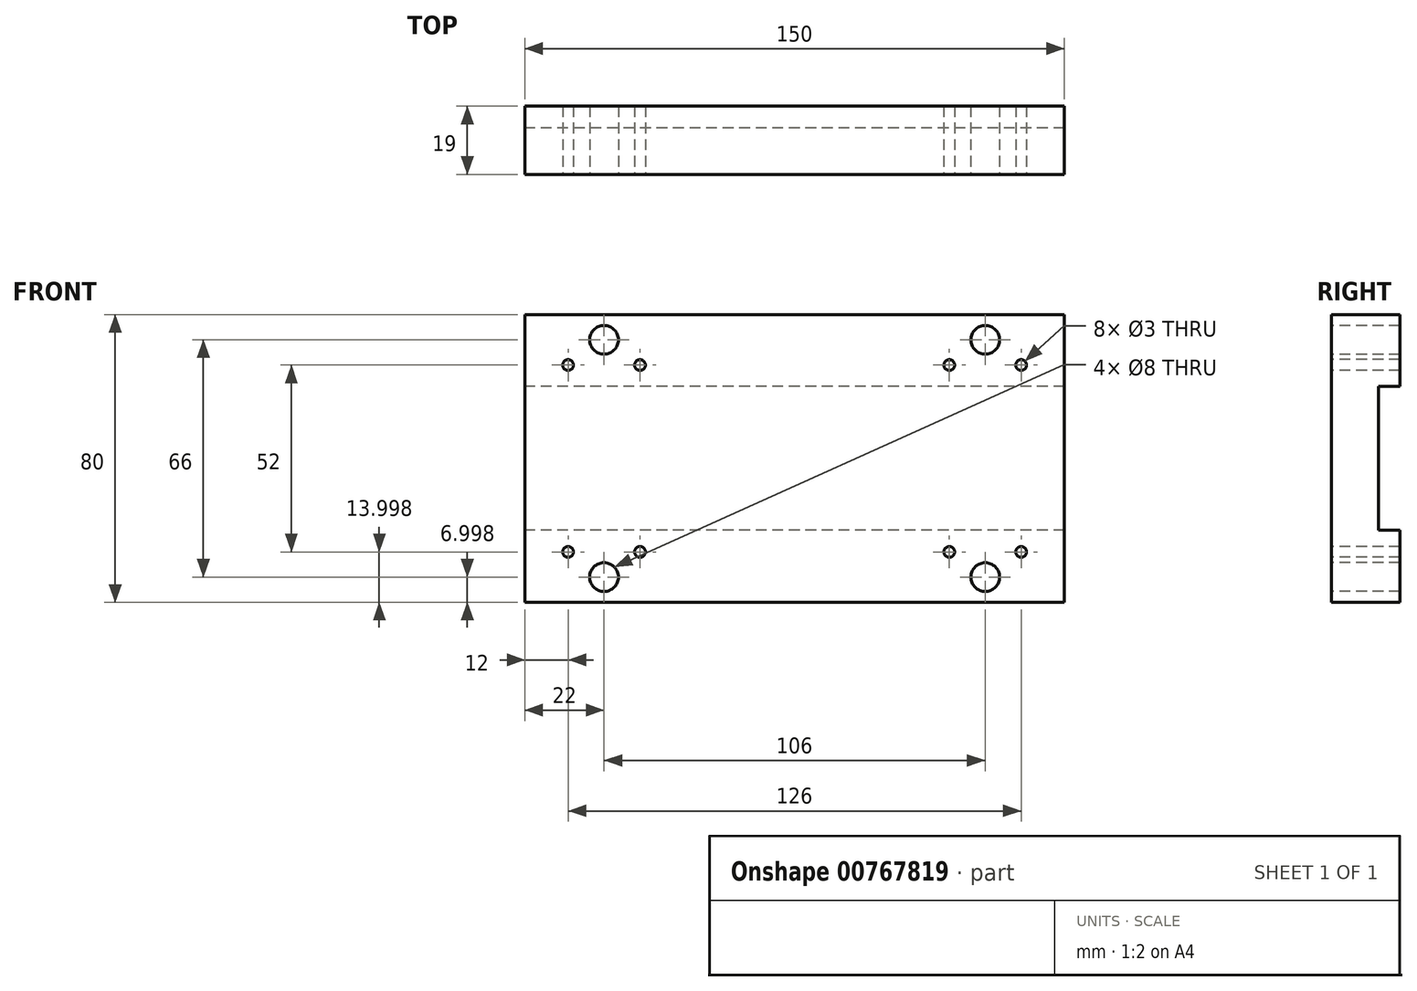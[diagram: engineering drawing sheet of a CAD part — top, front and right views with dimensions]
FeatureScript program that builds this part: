
annotation { "Feature Type Name" : "Feature", "Feature Type Description" : "" }
export const myFeature = defineFeature(function(context is Context, id is Id, definition is map)
    precondition{}
    {
        {
            var Q0;
            Q0=qCreatedBy(makeId("Right.planeOp"),FACE);
            var sketch = newSketch(context, id + "F0", { "sketchPlane" : qUnion([Q0])});
            skLineSegment(sketch, "E0.bottom", {"start": v(0, 43.24) * mm, "end": v(-19, 43.24) * mm});
            skLineSegment(sketch, "E0.top", {"start": v(0, -36.76) * mm, "end": v(-19, -36.76) * mm});
            skLineSegment(sketch, "E0.left", {"start": v(0, 43.24) * mm, "end": v(0, 23.24) * mm});
            skLineSegment(sketch, "E0.right", {"start": v(-19, 43.24) * mm, "end": v(-19, -36.76) * mm});
            skLineSegment(sketch, "E1.bottom", {"start": v(0, 23.24) * mm, "end": v(-6, 23.24) * mm});
            skLineSegment(sketch, "E1.top", {"start": v(0, -16.76) * mm, "end": v(-6, -16.76) * mm});
            skLineSegment(sketch, "E1.right", {"start": v(-6, 23.24) * mm, "end": v(-6, -16.76) * mm});
            skLineSegment(sketch, "E2.trimOffspring", {"start": v(0, -16.76) * mm, "end": v(0, -36.76) * mm});
            skSolve(sketch);
        }
        {
            var Q0;
            Q0=makeQuery(id+"F0.imprint","IMPRINT",FACE,{"disambiguationData":[TD([[makeQuery(id+"F0.imprint","IMPRINT",EDGE,{"derivedFrom":sQuery(id+"F0.wireOp",EDGE,"E0.bottom")}),1.0]])]});
            extrude(context, id + "F1", {"entities" : qUnion([Q0]), "depth" : 150 * mm, "offsetDistance" : 25 * mm});
        }
        {
            var Q0;
            Q0=makeQuery(id+"F1.opExtrude","SWEPT_FACE",FACE,{"disambiguationData":[OSD([sQuery(id+"F0.wireOp",EDGE,"E0.right")])]});
            var sketch = newSketch(context, id + "F2", { "sketchPlane" : qUnion([Q0])});
            skLineSegment(sketch, "E3", {"start": v(0, 29.24) * mm, "end": v(150, 29.24) * mm, "construction": true});
            skLineSegment(sketch, "E4", {"start": v(12, 43.24) * mm, "end": v(12, -36.76) * mm, "construction": true});
            skLineSegment(sketch, "E5", {"start": v(0, -22.76) * mm, "end": v(150, -22.76) * mm, "construction": true});
            skLineSegment(sketch, "E6", {"start": v(138, 43.24) * mm, "end": v(138, -36.76) * mm, "construction": true});
            skPoint(sketch, "E7", {"position": v(12, 29.24) * mm});
            skPoint(sketch, "E8", {"position": v(138, 29.24) * mm});
            skPoint(sketch, "E9", {"position": v(138, -22.76) * mm});
            skPoint(sketch, "E10", {"position": v(12, -22.76) * mm});
            skLineSegment(sketch, "E11", {"start": v(118, 43.24) * mm, "end": v(118, -36.76) * mm, "construction": true});
            skLineSegment(sketch, "E12", {"start": v(32, 43.24) * mm, "end": v(32, -36.76) * mm, "construction": true});
            skPoint(sketch, "E13", {"position": v(118, 29.24) * mm});
            skPoint(sketch, "E14", {"position": v(32, 29.24) * mm});
            skPoint(sketch, "E15", {"position": v(32, -22.76) * mm});
            skPoint(sketch, "E16", {"position": v(118, -22.76) * mm});
            skLineSegment(sketch, "E17", {"start": v(138, 43.24) * mm, "end": v(118, 29.24) * mm});
            skLineSegment(sketch, "E18", {"start": v(32, 29.24) * mm, "end": v(12, 43.24) * mm});
            skLineSegment(sketch, "E19", {"start": v(32, -22.76) * mm, "end": v(12, -36.76) * mm});
            skLineSegment(sketch, "E20", {"start": v(118, -22.76) * mm, "end": v(138, -36.76) * mm});
            skPoint(sketch, "E21", {"position": v(128, 36.24) * mm});
            skPoint(sketch, "E22", {"position": v(22, 36.24) * mm});
            skPoint(sketch, "E23", {"position": v(22, -29.76) * mm});
            skPoint(sketch, "E24", {"position": v(128, -29.76) * mm});
            skSolve(sketch);
        }
        {
            var Q0;
            Q0=sQuery(id+"F2.wireOp",VERTEX,"E7");
            var Q1;
            Q1=sQuery(id+"F2.wireOp",VERTEX,"E8");
            var Q2;
            Q2=sQuery(id+"F2.wireOp",VERTEX,"E10");
            var Q3;
            Q3=sQuery(id+"F2.wireOp",VERTEX,"E9");
            var Q4;
            Q4=sQuery(id+"F2.wireOp",VERTEX,"E13");
            var Q5;
            Q5=sQuery(id+"F2.wireOp",VERTEX,"E16");
            var Q6;
            Q6=sQuery(id+"F2.wireOp",VERTEX,"E14");
            var Q7;
            Q7=sQuery(id+"F2.wireOp",VERTEX,"E15");
            var Q8;
            Q8=makeQuery(id+"F1.opExtrude","SWEPT_BODY",BODY,{"disambiguationData":[OSD([sQuery(id+"F0.wireOp",EDGE,"E0.bottom"),sQuery(id+"F0.wireOp",EDGE,"E0.top"),sQuery(id+"F0.wireOp",EDGE,"E0.left"),sQuery(id+"F0.wireOp",EDGE,"E0.right"),sQuery(id+"F0.wireOp",EDGE,"E1.bottom"),sQuery(id+"F0.wireOp",EDGE,"E1.top"),sQuery(id+"F0.wireOp",EDGE,"E1.right"),sQuery(id+"F0.wireOp",EDGE,"E2.trimOffspring")])]});
            hole(context, id + "F3", {"style" : HoleStyle.SIMPLE, "endStyle" : HoleEndStyle.THROUGH, "holeDiameter" : 3 * mm, "majorDiameter" : 5 * mm, "isTappedThrough" : true, "tappedDepth" : 12 * mm, "tapClearance" : 3, "locations" : qUnion([Q0, Q1, Q2, Q3, Q4, Q5, Q6, Q7]), "scope" : qUnion([Q8])});
        }
        {
            var Q0;
            Q0=sQuery(id+"F2.wireOp",VERTEX,"E21");
            var Q1;
            Q1=sQuery(id+"F2.wireOp",VERTEX,"E22");
            var Q2;
            Q2=sQuery(id+"F2.wireOp",VERTEX,"E23");
            var Q3;
            Q3=sQuery(id+"F2.wireOp",VERTEX,"E24");
            var Q4;
            Q4=makeQuery(id+"F1.opExtrude","SWEPT_BODY",BODY,{"disambiguationData":[OSD([sQuery(id+"F0.wireOp",EDGE,"E0.bottom"),sQuery(id+"F0.wireOp",EDGE,"E0.top"),sQuery(id+"F0.wireOp",EDGE,"E0.left"),sQuery(id+"F0.wireOp",EDGE,"E0.right"),sQuery(id+"F0.wireOp",EDGE,"E1.bottom"),sQuery(id+"F0.wireOp",EDGE,"E1.top"),sQuery(id+"F0.wireOp",EDGE,"E1.right"),sQuery(id+"F0.wireOp",EDGE,"E2.trimOffspring")])]});
            hole(context, id + "F4", {"style" : HoleStyle.SIMPLE, "endStyle" : HoleEndStyle.THROUGH, "holeDiameter" : 8 * mm, "majorDiameter" : 5 * mm, "isTappedThrough" : true, "tappedDepth" : 12 * mm, "tapClearance" : 3, "locations" : qUnion([Q0, Q1, Q2, Q3]), "scope" : qUnion([Q4])});
        }
    });
